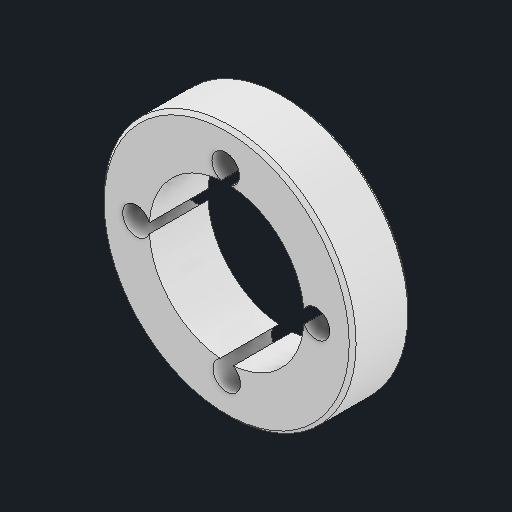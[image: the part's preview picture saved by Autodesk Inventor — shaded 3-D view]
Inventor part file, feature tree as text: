
AUTODESK INVENTOR PART (.ipt)
format: ipt  version: 2022 (Build 260153070, 153G)  size: 136,704 bytes
history: native  units: mm
features: sketch x2, other x1, extrude x1, chamfer x1, hole x1
ambient origin geometry x8: Origin, YZ Plane, XZ Plane, XY Plane, X Axis, Y Axis, Z Axis, Center Point
bodies: Body1 (feature_tree)
feature tree (6):
  other  "Твердое тело1"
  extrude  "Выдавливание1"  Depth=17.0mm TaperAngle=0.0deg
  chamfer  "Фаска1"  Distance=1.0mm Angle=45.0deg
  hole  "Отверстие1"  [1 undecoded]
  sketch  "Эскиз1"
  sketch  "Эскиз2"
note: 1 required parameter value undecoded (feature->parameter linkage not recoverable at this tier; creation-order binding heuristic only, values carry confidence <= 0.55)
